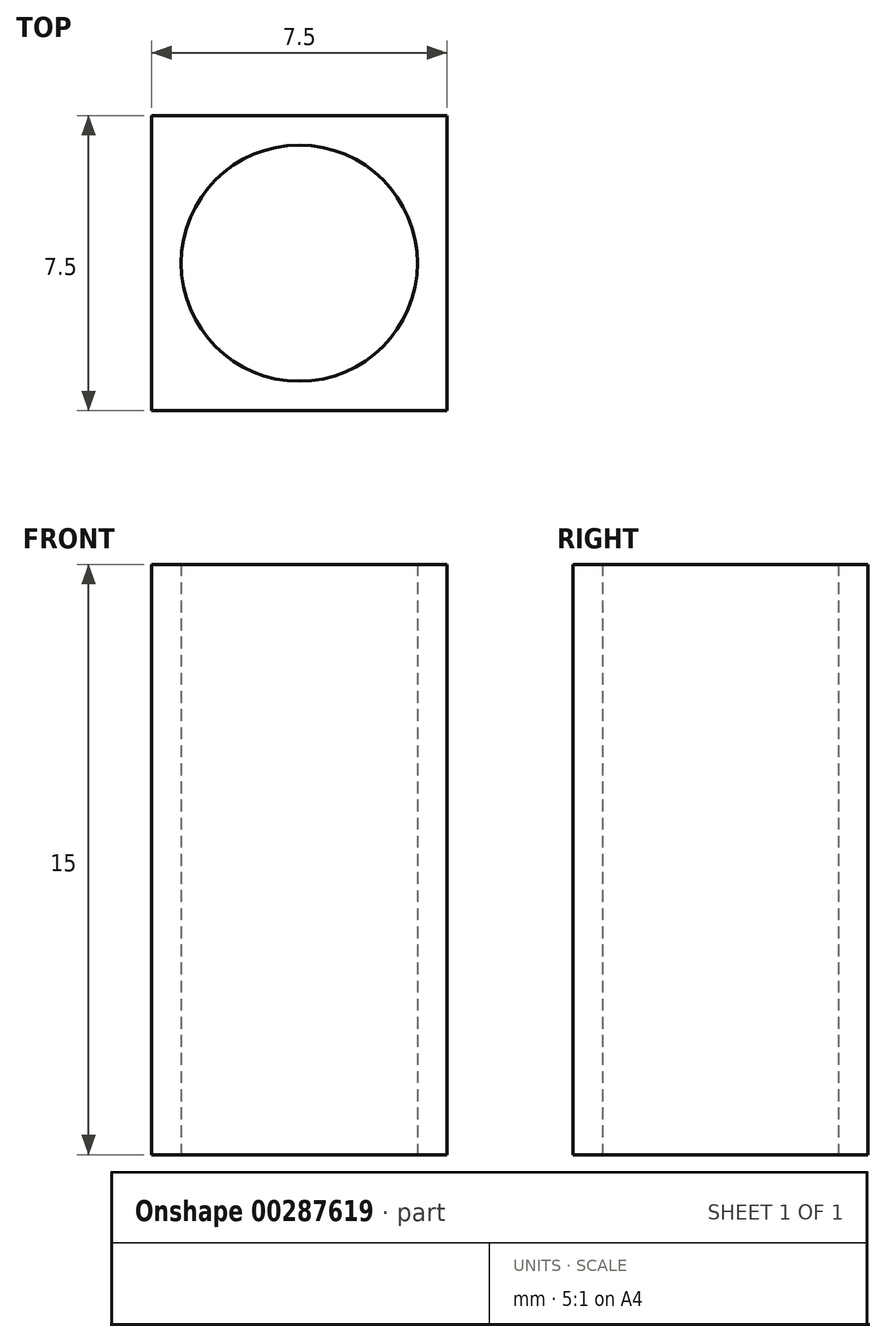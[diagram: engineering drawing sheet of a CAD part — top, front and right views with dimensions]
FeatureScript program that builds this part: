
annotation { "Feature Type Name" : "Feature", "Feature Type Description" : "" }
export const myFeature = defineFeature(function(context is Context, id is Id, definition is map)
    precondition{}
    {
        {
            var Q0;
            Q0=qCreatedBy(makeId("Top.planeOp"),FACE);
            var sketch = newSketch(context, id + "F0", { "sketchPlane" : qUnion([Q0])});
            skCircle(sketch, "E0", {"center": v(0, 0) * mm, "radius": 3 * mm});
            skLineSegment(sketch, "E1.bottom", {"start": v(3.75, -3.75) * mm, "end": v(-3.75, -3.75) * mm});
            skLineSegment(sketch, "E1.top", {"start": v(3.75, 3.75) * mm, "end": v(-3.75, 3.75) * mm});
            skLineSegment(sketch, "E1.left", {"start": v(3.75, -3.75) * mm, "end": v(3.75, 3.75) * mm});
            skLineSegment(sketch, "E1.right", {"start": v(-3.75, -3.75) * mm, "end": v(-3.75, 3.75) * mm});
            skSolve(sketch);
        }
        {
            var Q0;
            Q0=makeQuery(id+"F0.imprint","IMPRINT",FACE,{"disambiguationData":[TD([[makeQuery(id+"F0.imprint","IMPRINT",EDGE,{"derivedFrom":sQuery(id+"F0.wireOp",EDGE,"E0")}),-1.0]])]});
            extrude(context, id + "F1", {"entities" : qUnion([Q0]), "depth" : 15 * mm, "offsetDistance" : 25 * mm});
        }
    });
